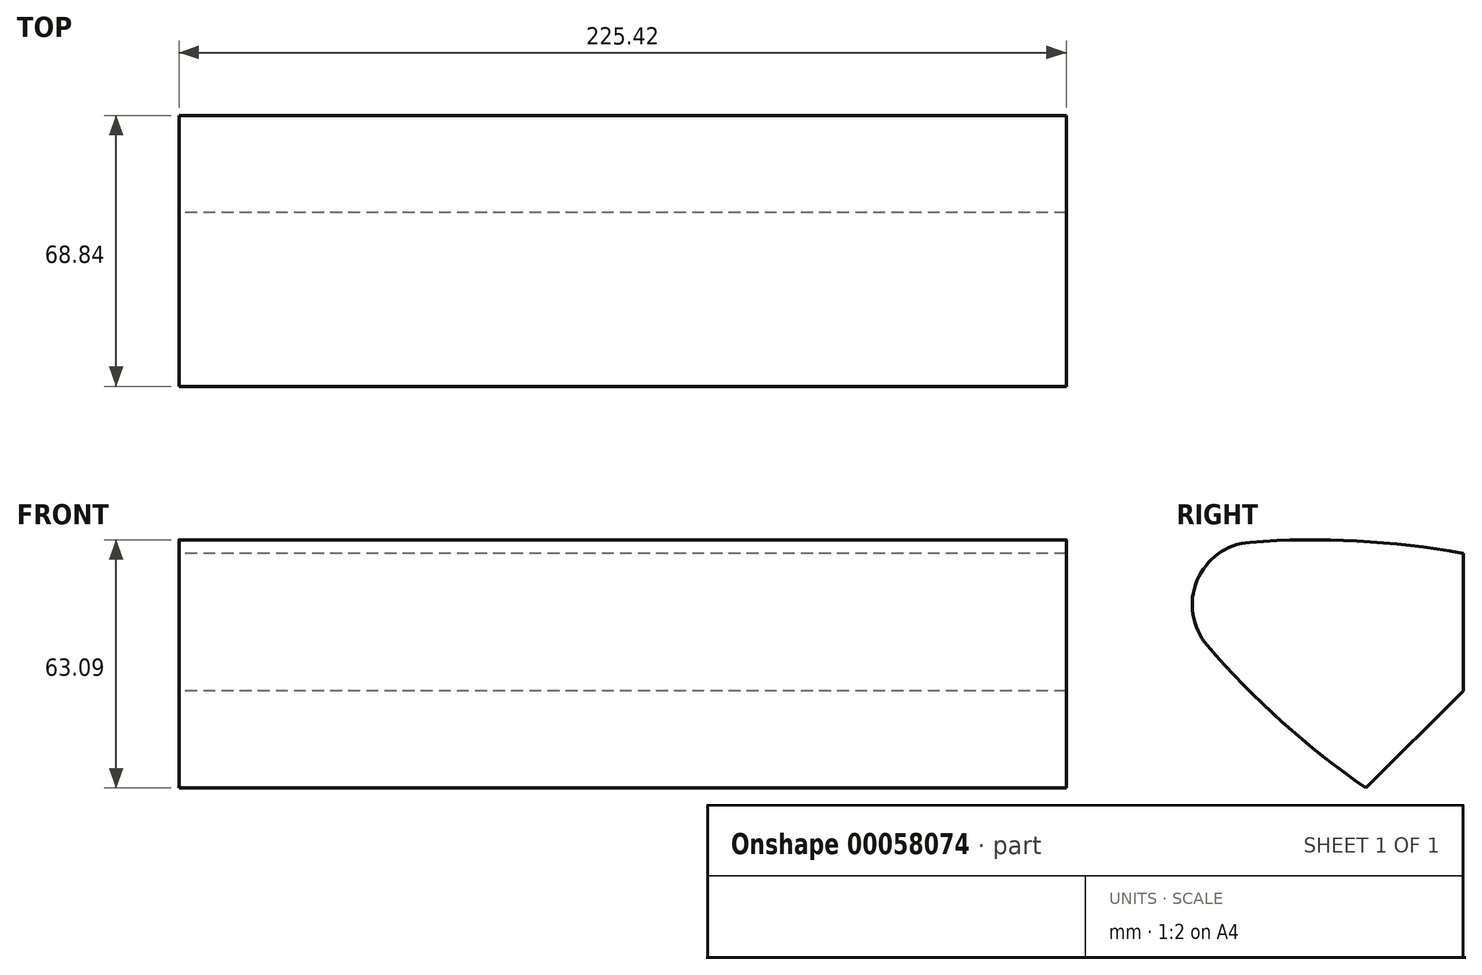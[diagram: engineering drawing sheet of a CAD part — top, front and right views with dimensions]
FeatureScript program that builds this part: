
annotation { "Feature Type Name" : "Feature", "Feature Type Description" : "" }
export const myFeature = defineFeature(function(context is Context, id is Id, definition is map)
    precondition{}
    {
        {
            var Q0;
            Q0=qCreatedBy(makeId("Right.planeOp"),FACE);
            var sketch = newSketch(context, id + "F0", { "sketchPlane" : qUnion([Q0])});
            skLineSegment(sketch, "E0", {"start": v(-24.7, -24.7) * mm, "end": v(0, 0) * mm});
            skLineSegment(sketch, "E1", {"start": v(0, 0) * mm, "end": v(0, 34.93) * mm});
            skLineSegment(sketch, "E2", {"start": v(-96.53, 39.98) * mm, "end": v(0, 34.92) * mm, "construction": true});
            skLineSegment(sketch, "E3", {"start": v(0, 0) * mm, "end": v(-96.53, 39.98) * mm, "construction": true});
            skLineSegment(sketch, "E4", {"start": v(0, 34.93) * mm, "end": v(-24.7, -24.7) * mm, "construction": true});
            skPoint(sketch, "E5", {"position": v(-12.35, 5.11) * mm});
            skLineSegment(sketch, "E6", {"start": v(-96.53, 39.98) * mm, "end": v(-24.7, -24.7) * mm, "construction": true});
            skArc(sketch, "E7", {"start": v(0, 34.93) * mm, "mid": v(-27, 38.1) * mm, "end": v(-54.19, 37.76) * mm});
            skArc(sketch, "E8", {"start": v(-54.19, 37.76) * mm, "mid": v(-67.63, 28.01) * mm, "end": v(-65.02, 11.61) * mm});
            skArc(sketch, "E9", {"start": v(-65.02, 11.61) * mm, "mid": v(-46.03, -7.85) * mm, "end": v(-24.7, -24.7) * mm});
            skSolve(sketch);
        }
        {
            var Q0;
            Q0=qSketchRegion(id+"F0",true);
            extrude(context, id + "F1", {"entities" : qUnion([Q0]), "endBound" : BoundingType.SYMMETRIC, "depth" : 225.42 * mm});
        }
    });
